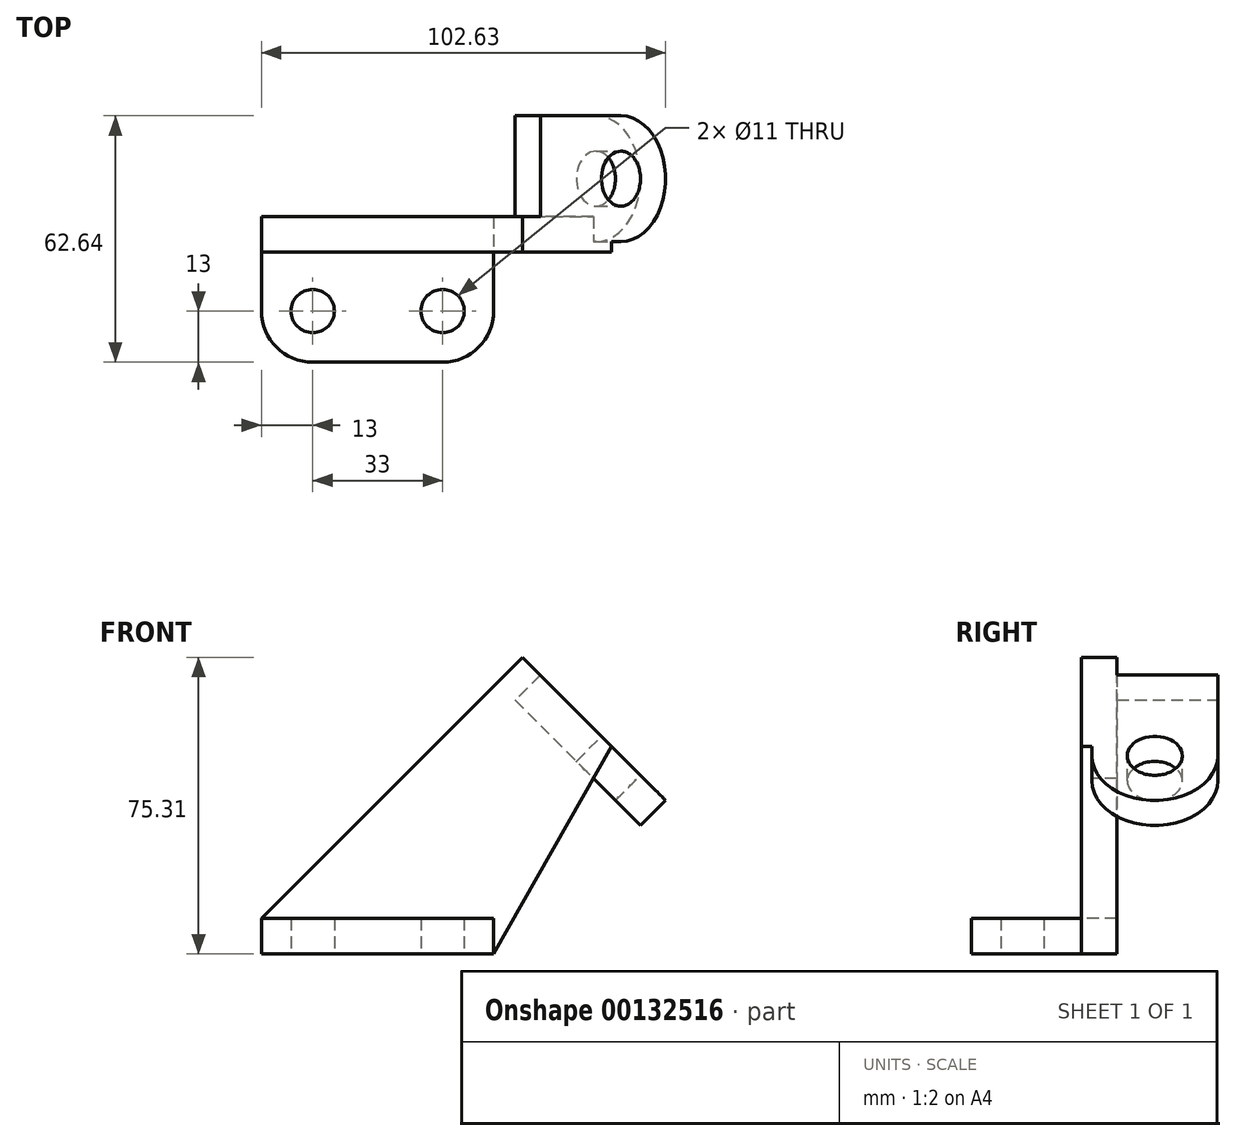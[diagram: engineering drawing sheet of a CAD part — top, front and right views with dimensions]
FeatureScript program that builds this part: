
annotation { "Feature Type Name" : "Feature", "Feature Type Description" : "" }
export const myFeature = defineFeature(function(context is Context, id is Id, definition is map)
    precondition{}
    {
        {
            var Q0;
            Q0=qCreatedBy(makeId("Top.planeOp"),FACE);
            var sketch = newSketch(context, id + "F0", { "sketchPlane" : qUnion([Q0])});
            skLineSegment(sketch, "E0", {"start": v(0, 0) * mm, "end": v(59, 0) * mm});
            skLineSegment(sketch, "E1", {"start": v(59, 0) * mm, "end": v(59, -24) * mm});
            skLineSegment(sketch, "E2", {"start": v(0, 0) * mm, "end": v(0, -24) * mm});
            skLineSegment(sketch, "E3", {"start": v(13, -37) * mm, "end": v(46, -37) * mm});
            skArc(sketch, "E4", {"start": v(0, -24) * mm, "mid": v(3.8, -33.2) * mm, "end": v(13, -37) * mm});
            skArc(sketch, "E5", {"start": v(46, -37) * mm, "mid": v(55.2, -33.2) * mm, "end": v(59, -24) * mm});
            skLineSegment(sketch, "E6", {"start": v(-9.77, -24) * mm, "end": v(70.67, -24) * mm, "construction": true});
            skCircle(sketch, "E7", {"center": v(13, -24) * mm, "radius": 5.5 * mm});
            skCircle(sketch, "E8", {"center": v(46, -24) * mm, "radius": 5.5 * mm});
            skSolve(sketch);
        }
        {
            var Q0;
            Q0 = qSketchRegion(id + "F0", true);
            extrude(context, id + "F1", {"entities" : qUnion([Q0]), "depth" : 9 * mm});
        }
        {
            var Q0;
            Q0=makeQuery(id+"F1.opExtrude","SWEPT_FACE",FACE,{"disambiguationData":[OSD([sQuery(id+"F0.wireOp",EDGE,"E0")])]});
            var sketch = newSketch(context, id + "F2", { "sketchPlane" : qUnion([Q0])});
            skLineSegment(sketch, "E9", {"start": v(0, 9) * mm, "end": v(-66.31, 75.31) * mm});
            skLineSegment(sketch, "E10", {"start": v(-88.94, 52.69) * mm, "end": v(-66.31, 75.31) * mm});
            skLineSegment(sketch, "E11", {"start": v(-88.94, 52.69) * mm, "end": v(-59, 0) * mm});
            skLineSegment(sketch, "E12", {"start": v(-59, 0) * mm, "end": v(0, 0) * mm});
            skLineSegment(sketch, "E13", {"start": v(0, 0) * mm, "end": v(0, 9) * mm});
            skLineSegment(sketch, "E14", {"start": v(-62.89, 64) * mm, "end": v(-92.37, 64) * mm, "construction": true});
            skPoint(sketch, "E14.endSnap0", {"position": v(-77.63, 64) * mm});
            skSolve(sketch);
        }
        {
            var Q0;
            Q0 = qSketchRegion(id + "F2", true);
            extrude(context, id + "F3", {"entities" : qUnion([Q0]), "operationType" : NewBodyOperationType.ADD, "oppositeDirection" : true, "depth" : 9 * mm});
        }
        {
            var Q0;
            Q0=makeQuery(id+"F3.opExtrude","SWEPT_FACE",FACE,{"disambiguationData":[OSD([sQuery(id+"F2.wireOp",EDGE,"E10")])]});
            var sketch = newSketch(context, id + "F4", { "sketchPlane" : qUnion([Q0])});
            skLineSegment(sketch, "E15", {"start": v(25.64, 0) * mm, "end": v(25.64, -29) * mm});
            skArc(sketch, "E16", {"start": v(-6.36, -29) * mm, "mid": v(9.64, -45) * mm, "end": v(25.64, -29) * mm});
            skCircle(sketch, "E17", {"center": v(9.64, -29) * mm, "radius": 7 * mm});
            skLineSegment(sketch, "E18", {"start": v(-6.36, -29) * mm, "end": v(-6.36, 0) * mm});
            skLineSegment(sketch, "E19", {"start": v(-6.36, 0) * mm, "end": v(25.64, 0) * mm});
            skSolve(sketch);
        }
        {
            var Q0;
            Q0 = qSketchRegion(id + "F4", true);
            extrude(context, id + "F5", {"entities" : qUnion([Q0]), "operationType" : NewBodyOperationType.ADD, "oppositeDirection" : true, "depth" : 9 * mm});
        }
    });
